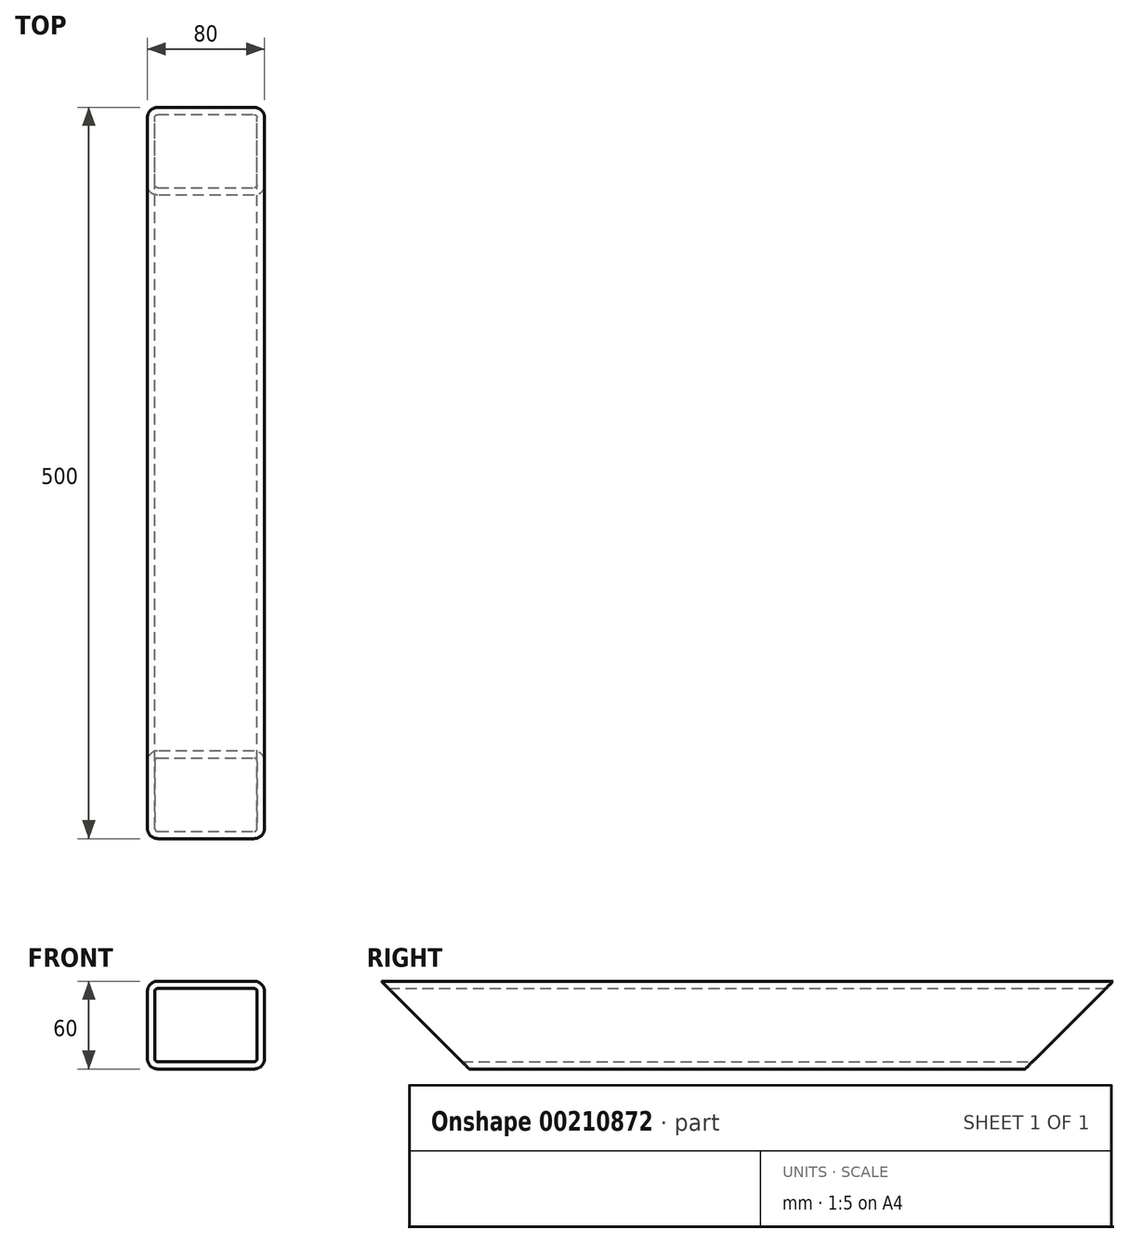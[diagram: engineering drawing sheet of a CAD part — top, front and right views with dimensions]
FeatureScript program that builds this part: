
annotation { "Feature Type Name" : "Feature", "Feature Type Description" : "" }
export const myFeature = defineFeature(function(context is Context, id is Id, definition is map)
    precondition{}
    {
        {
            var Q0;
            Q0=qCreatedBy(makeId("Front.planeOp"),FACE);
            var sketch = newSketch(context, id + "F0", { "sketchPlane" : qUnion([Q0])});
            skLineSegment(sketch, "E0.bottom", {"start": v(33, 30) * mm, "end": v(-33, 30) * mm});
            skLineSegment(sketch, "E0.top", {"start": v(33, -30) * mm, "end": v(-33, -30) * mm});
            skLineSegment(sketch, "E0.left", {"start": v(40, 23) * mm, "end": v(40, -23) * mm});
            skLineSegment(sketch, "E0.right", {"start": v(-40, 23) * mm, "end": v(-40, -23) * mm});
            skPoint(sketch, "E0.middle", {"position": v(0, 0) * mm});
            skLineSegment(sketch, "E1.bottom", {"start": v(33, 25) * mm, "end": v(-33, 25) * mm});
            skLineSegment(sketch, "E1.top", {"start": v(33, -25) * mm, "end": v(-33, -25) * mm});
            skLineSegment(sketch, "E1.left", {"start": v(35, 23) * mm, "end": v(35, -23) * mm});
            skLineSegment(sketch, "E1.right", {"start": v(-35, 23) * mm, "end": v(-35, -23) * mm});
            skPoint(sketch, "E2.visualSharp", {"position": v(-40, 30) * mm});
            skArc(sketch, "E2.filletArc", {"start": v(-33, 30) * mm, "mid": v(-37.95, 27.95) * mm, "end": v(-40, 23) * mm});
            skPoint(sketch, "E3.visualSharp", {"position": v(-40, -30) * mm});
            skArc(sketch, "E3.filletArc", {"start": v(-40, -23) * mm, "mid": v(-37.95, -27.95) * mm, "end": v(-33, -30) * mm});
            skPoint(sketch, "E4.visualSharp", {"position": v(40, -30) * mm});
            skArc(sketch, "E4.filletArc", {"start": v(33, -30) * mm, "mid": v(37.95, -27.95) * mm, "end": v(40, -23) * mm});
            skPoint(sketch, "E5.visualSharp", {"position": v(40, 30) * mm});
            skArc(sketch, "E5.filletArc", {"start": v(40, 23) * mm, "mid": v(37.95, 27.95) * mm, "end": v(33, 30) * mm});
            skPoint(sketch, "E6.visualSharp", {"position": v(-35, -25) * mm});
            skArc(sketch, "E6.filletArc", {"start": v(-35, -23) * mm, "mid": v(-34.41, -24.41) * mm, "end": v(-33, -25) * mm});
            skPoint(sketch, "E7.visualSharp", {"position": v(35, 25) * mm});
            skArc(sketch, "E7.filletArc", {"start": v(35, 23) * mm, "mid": v(34.41, 24.41) * mm, "end": v(33, 25) * mm});
            skPoint(sketch, "E8.visualSharp", {"position": v(35, -25) * mm});
            skArc(sketch, "E8.filletArc", {"start": v(33, -25) * mm, "mid": v(34.41, -24.41) * mm, "end": v(35, -23) * mm});
            skPoint(sketch, "E9.visualSharp", {"position": v(-35, 25) * mm});
            skArc(sketch, "E9.filletArc", {"start": v(-33, 25) * mm, "mid": v(-34.41, 24.41) * mm, "end": v(-35, 23) * mm});
            skSolve(sketch);
        }
        {
            var Q0;
            Q0=makeQuery(id+"F0.imprint","IMPRINT",FACE,{"disambiguationData":[TD([[makeQuery(id+"F0.imprint","IMPRINT",EDGE,{"derivedFrom":sQuery(id+"F0.wireOp",EDGE,"E0.bottom")}),1.0]])]});
            extrude(context, id + "F1", {"entities" : qUnion([Q0]), "endBound" : BoundingType.SYMMETRIC, "depth" : 500 * mm});
        }
        {
            var Q0;
            Q0=makeQuery(id+"F1.opExtrude","SWEPT_FACE",FACE,{"disambiguationData":[OSD([sQuery(id+"F0.wireOp",EDGE,"E0.right")])]});
            var sketch = newSketch(context, id + "F2", { "sketchPlane" : qUnion([Q0])});
            skLineSegment(sketch, "E10.0", {"start": v(-190, -30) * mm, "end": v(-250, -30) * mm});
            skPoint(sketch, "E11.0", {"position": v(-250, 30) * mm});
            skLineSegment(sketch, "E12", {"start": v(-250, 30) * mm, "end": v(-250, -30) * mm});
            skLineSegment(sketch, "E13", {"start": v(-250, 30) * mm, "end": v(-190, -30) * mm});
            skPoint(sketch, "E14.orphan", {"position": v(250, -30) * mm});
            skLineSegment(sketch, "E15.MirrorCS", {"start": v(250, 30) * mm, "end": v(250, -30) * mm});
            skLineSegment(sketch, "E16.MirrorCS", {"start": v(250, 30) * mm, "end": v(190, -30) * mm});
            skLineSegment(sketch, "E17.MirrorCS", {"start": v(190, -30) * mm, "end": v(250, -30) * mm});
            skSolve(sketch);
        }
        {
            var Q0;
            {var subQ0=sQuery(id+"F2.wireOp",EDGE,"E10.0");Q0=makeQuery(id+"F2.imprint","IMPRINT",FACE,{"disambiguationData":[TD([[makeQuery(id+"F2.imprint","IMPRINT",EDGE,{"derivedFrom":subQ0}),-1.0]])]});}
            var Q1;
            {var subQ0=sQuery(id+"F2.wireOp",EDGE,"E12");var subQ1=sQuery(id+"F0.wireOp",EDGE,"E0.right");var subQ2=makeQuery(id+"F1.opExtrude","SWEPT_EDGE",EDGE,{"disambiguationData":[OSD([subQ1,sQuery(id+"F0.wireOp",EDGE,"E2.filletArc")])]});var subQ3=makeQuery(id+"F2.imprint","INTERSECT",VERTEX,{"derivedFrom":[subQ2,subQ0]});Q1=makeQuery(id+"F2.imprint","IMPRINT",FACE,{"disambiguationData":[TD([[makeQuery(id+"F2.imprint","IMPRINT",EDGE,{"disambiguationData":[TD([[subQ3,-1.0]])],"derivedFrom":subQ0}),1.0]])]});}
            var Q2;
            {var subQ0=sQuery(id+"F2.wireOp",EDGE,"E12");var subQ3=sQuery(id+"F2.wireOp",EDGE,"E13");var subQ4=makeQuery(id+"F2.imprint","INTERSECT",VERTEX,{"derivedFrom":[subQ0,subQ3]});Q2=makeQuery(id+"F2.imprint","IMPRINT",FACE,{"disambiguationData":[TD([[makeQuery(id+"F2.imprint","IMPRINT",EDGE,{"disambiguationData":[TD([[subQ4,-1.0]])],"derivedFrom":subQ0}),1.0]])]});}
            var Q3;
            {var subQ0=sQuery(id+"F2.wireOp",EDGE,"E15.MirrorCS");var subQ1=sQuery(id+"F0.wireOp",EDGE,"E0.right");var subQ2=makeQuery(id+"F1.opExtrude","SWEPT_EDGE",EDGE,{"disambiguationData":[OSD([subQ1,sQuery(id+"F0.wireOp",EDGE,"E2.filletArc")])]});var subQ3=makeQuery(id+"F2.imprint","INTERSECT",VERTEX,{"derivedFrom":[subQ2,subQ0]});Q3=makeQuery(id+"F2.imprint","IMPRINT",FACE,{"disambiguationData":[TD([[makeQuery(id+"F2.imprint","IMPRINT",EDGE,{"disambiguationData":[TD([[subQ3,-1.0]])],"derivedFrom":subQ0}),-1.0]])]});}
            var Q4;
            {var subQ3=sQuery(id+"F2.wireOp",EDGE,"E17.MirrorCS");Q4=makeQuery(id+"F2.imprint","IMPRINT",FACE,{"disambiguationData":[TD([[makeQuery(id+"F2.imprint","IMPRINT",EDGE,{"derivedFrom":subQ3}),1.0]])]});}
            var Q5;
            {var subQ0=sQuery(id+"F2.wireOp",EDGE,"E15.MirrorCS");var subQ3=sQuery(id+"F2.wireOp",EDGE,"E16.MirrorCS");var subQ4=makeQuery(id+"F2.imprint","INTERSECT",VERTEX,{"derivedFrom":[subQ0,subQ3]});Q5=makeQuery(id+"F2.imprint","IMPRINT",FACE,{"disambiguationData":[TD([[makeQuery(id+"F2.imprint","IMPRINT",EDGE,{"disambiguationData":[TD([[subQ4,-1.0]])],"derivedFrom":subQ0}),-1.0]])]});}
            extrude(context, id + "F3", {"entities" : qUnion([Q0, Q1, Q2, Q3, Q4, Q5]), "operationType" : NewBodyOperationType.REMOVE, "oppositeDirection" : true, "depth" : 200 * mm});
        }
    });
